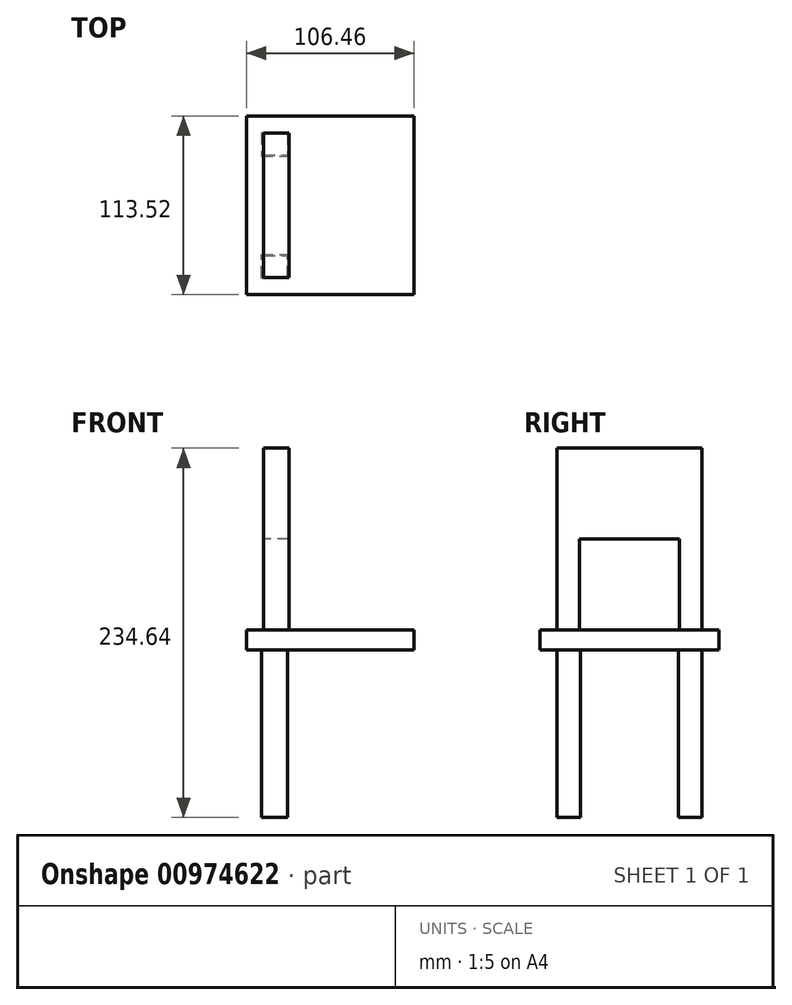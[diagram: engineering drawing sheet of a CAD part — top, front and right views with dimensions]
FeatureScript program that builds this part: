
annotation { "Feature Type Name" : "Feature", "Feature Type Description" : "" }
export const myFeature = defineFeature(function(context is Context, id is Id, definition is map)
    precondition{}
    {
        {
            var Q0;
            Q0=qCreatedBy(makeId("Top.planeOp"),FACE);
            var sketch = newSketch(context, id + "F0", { "sketchPlane" : qUnion([Q0])});
            skLineSegment(sketch, "E0.bottom", {"start": v(-50.21, 46.46) * mm, "end": v(56.25, 46.46) * mm});
            skLineSegment(sketch, "E0.top", {"start": v(-50.21, -56.76) * mm, "end": v(56.25, -56.76) * mm});
            skLineSegment(sketch, "E0.left", {"start": v(-50.21, 46.46) * mm, "end": v(-50.21, -56.76) * mm});
            skLineSegment(sketch, "E0.right", {"start": v(56.25, 46.46) * mm, "end": v(56.25, -56.76) * mm});
            skSolve(sketch);
        }
        {
            var Q0;
            Q0=makeQuery(id+"F0.imprint","IMPRINT",FACE,{"disambiguationData":[TD([[makeQuery(id+"F0.imprint","IMPRINT",EDGE,{"derivedFrom":sQuery(id+"F0.wireOp",EDGE,"E0.bottom")}),-1.0]])]});
            extrude(context, id + "F1", {"entities" : qUnion([Q0]), "depth" : 12.7 * mm, "offsetDistance" : 25.4 * mm});
        }
        {
            var Q0;
            Q0=makeQuery(id+"F1.opExtrude","CAP_FACE",FACE,{"disambiguationData":[OSD([sQuery(id+"F0.wireOp",EDGE,"E0.bottom"),sQuery(id+"F0.wireOp",EDGE,"E0.top"),sQuery(id+"F0.wireOp",EDGE,"E0.left"),sQuery(id+"F0.wireOp",EDGE,"E0.right")])],"isStart":false});
            var sketch = newSketch(context, id + "F2", { "sketchPlane" : qUnion([Q0])});
            skLineSegment(sketch, "E1", {"start": v(-39.56, -31.77) * mm, "end": v(-23.18, -31.77) * mm});
            skLineSegment(sketch, "E2", {"start": v(-23.18, -31.77) * mm, "end": v(-23.18, -45.95) * mm});
            skLineSegment(sketch, "E3", {"start": v(-23.18, -45.95) * mm, "end": v(-39.56, -45.95) * mm});
            skLineSegment(sketch, "E4", {"start": v(-39.56, -45.95) * mm, "end": v(-39.56, -31.77) * mm});
            skSolve(sketch);
        }
        {
            var Q0;
            Q0=makeQuery(id+"F2.imprint","IMPRINT",FACE,{"disambiguationData":[TD([[makeQuery(id+"F2.imprint","IMPRINT",EDGE,{"derivedFrom":sQuery(id+"F2.wireOp",EDGE,"E1")}),-1.0]])]});
            extrude(context, id + "F3", {"entities" : qUnion([Q0]), "operationType" : NewBodyOperationType.ADD, "depth" : 115.48 * mm, "offsetDistance" : 25.4 * mm});
        }
        {
            var Q0;
            Q0=makeQuery(id+"F3.opExtrude","SWEPT_FACE",FACE,{"disambiguationData":[OSD([sQuery(id+"F2.wireOp",EDGE,"E1")])]});
            var sketch = newSketch(context, id + "F4", { "sketchPlane" : qUnion([Q0])});
            skLineSegment(sketch, "E5", {"start": v(23.18, 70.44) * mm, "end": v(39.56, 70.44) * mm});
            skSolve(sketch);
        }
        {
            var Q0;
            {var subQ0=sQuery(id+"F4.wireOp",EDGE,"E5");Q0=makeQuery(id+"F4.imprint","IMPRINT",FACE,{"disambiguationData":[TD([[makeQuery(id+"F4.imprint","IMPRINT",EDGE,{"derivedFrom":subQ0}),1.0]])]});}
            extrude(context, id + "F5", {"entities" : qUnion([Q0]), "operationType" : NewBodyOperationType.ADD, "depth" : 25.4 * mm, "offsetDistance" : 25.4 * mm});
        }
        {
            var Q0;
            Q0=makeQuery(id+"F1.opExtrude","SWEPT_BODY",BODY,{"disambiguationData":[OSD([sQuery(id+"F0.wireOp",EDGE,"E0.bottom"),sQuery(id+"F0.wireOp",EDGE,"E0.top"),sQuery(id+"F0.wireOp",EDGE,"E0.left"),sQuery(id+"F0.wireOp",EDGE,"E0.right")])]});
            var Q1;
            Q1=qCreatedBy(makeId("Front.planeOp"),FACE);
            mirror(context, id + "F6", {"operationType" : NewBodyOperationType.ADD, "entities" : qUnion([Q0]), "mirrorPlane" : qUnion([Q1])});
        }
        {
            var Q0;
            Q0=makeQuery(id+"F5.opExtrude","CAP_FACE",FACE,{"disambiguationData":[OSD([sQuery(id+"F2.wireOp",EDGE,"E1"),sQuery(id+"F2.wireOp",EDGE,"E2"),sQuery(id+"F2.wireOp",EDGE,"E4"),sQuery(id+"F4.wireOp",EDGE,"E5")])],"isStart":false});
            var Q1;
            Q1=makeQuery(id+"F6.opPattern","COPY",FACE,{"derivedFrom":makeQuery(id+"F5.opExtrude","CAP_FACE",FACE,{"disambiguationData":[OSD([sQuery(id+"F2.wireOp",EDGE,"E1"),sQuery(id+"F2.wireOp",EDGE,"E2"),sQuery(id+"F2.wireOp",EDGE,"E4"),sQuery(id+"F4.wireOp",EDGE,"E5")])],"isStart":false}),"instanceName":"1"});
            extrude(context, id + "F7", {"entities" : qUnion([Q0]), "operationType" : NewBodyOperationType.ADD, "endBound" : BoundingType.UP_TO_SURFACE, "depth" : 25.4 * mm, "endBoundEntityFace" : qUnion([Q1]), "offsetDistance" : 25.4 * mm});
        }
        {
            var Q0;
            {var subQ0=makeQuery(id+"F1.opExtrude","CAP_FACE",FACE,{"disambiguationData":[OSD([sQuery(id+"F0.wireOp",EDGE,"E0.bottom"),sQuery(id+"F0.wireOp",EDGE,"E0.top"),sQuery(id+"F0.wireOp",EDGE,"E0.left"),sQuery(id+"F0.wireOp",EDGE,"E0.right")])],"isStart":true});Q0=makeQuery(id+"F6.boolean.opBoolean","MERGE",FACE,{"derivedFrom":[subQ0,makeQuery(id+"F6.opPattern","COPY",FACE,{"derivedFrom":subQ0,"instanceName":"1"})]});}
            var sketch = newSketch(context, id + "F8", { "sketchPlane" : qUnion([Q0])});
            skLineSegment(sketch, "E6.bottom", {"start": v(-40.77, 46.05) * mm, "end": v(-24.2, 46.05) * mm});
            skLineSegment(sketch, "E6.top", {"start": v(-40.77, 31.2) * mm, "end": v(-24.2, 31.2) * mm});
            skLineSegment(sketch, "E6.left", {"start": v(-40.77, 46.05) * mm, "end": v(-40.77, 31.2) * mm});
            skLineSegment(sketch, "E6.right", {"start": v(-24.2, 46.05) * mm, "end": v(-24.2, 31.2) * mm});
            skSolve(sketch);
        }
        {
            var Q0;
            Q0=makeQuery(id+"F8.imprint","IMPRINT",FACE,{"disambiguationData":[TD([[makeQuery(id+"F8.imprint","IMPRINT",EDGE,{"derivedFrom":sQuery(id+"F8.wireOp",EDGE,"E6.bottom")}),-1.0]])]});
            extrude(context, id + "F9", {"entities" : qUnion([Q0]), "operationType" : NewBodyOperationType.ADD, "depth" : 106.46 * mm, "offsetDistance" : 25.4 * mm});
        }
        {
            var Q0;
            Q0=qCreatedBy(makeId("Top.planeOp"),FACE);
            var sketch = newSketch(context, id + "F10", { "sketchPlane" : qUnion([Q0])});
            skCircle(sketch, "E7", {"center": v(108.96, 20.27) * mm, "radius": 29.95 * mm});
            skSolve(sketch);
        }
        {
            var Q0;
            Q0=makeQuery(id+"F10.imprint","IMPRINT",FACE,{"disambiguationData":[TD([[makeQuery(id+"F10.imprint","IMPRINT",EDGE,{"derivedFrom":sQuery(id+"F10.wireOp",EDGE,"E7")}),1.0]])]});
            extrude(context, id + "F11", {"entities" : qUnion([Q0]), "depth" : 25.4 * mm, "offsetDistance" : 25.4 * mm});
        }
        {
            var Q0;
            Q0=makeQuery(id+"F11.opExtrude","SWEPT_BODY",BODY,{"disambiguationData":[OSD([sQuery(id+"F10.wireOp",EDGE,"E7")])]});
            deleteBodies(context, id + "F12", {"entities" : qUnion([Q0])});
        }
        {
            var Q0;
            Q0=makeQuery(id+"F1.opExtrude","SWEPT_BODY",BODY,{"disambiguationData":[OSD([sQuery(id+"F0.wireOp",EDGE,"E0.bottom"),sQuery(id+"F0.wireOp",EDGE,"E0.top"),sQuery(id+"F0.wireOp",EDGE,"E0.left"),sQuery(id+"F0.wireOp",EDGE,"E0.right")])]});
            var Q1;
            Q1=qCreatedBy(makeId("Front.planeOp"),FACE);
            mirror(context, id + "F13", {"operationType" : NewBodyOperationType.ADD, "entities" : qUnion([Q0]), "mirrorPlane" : qUnion([Q1])});
        }
    });
